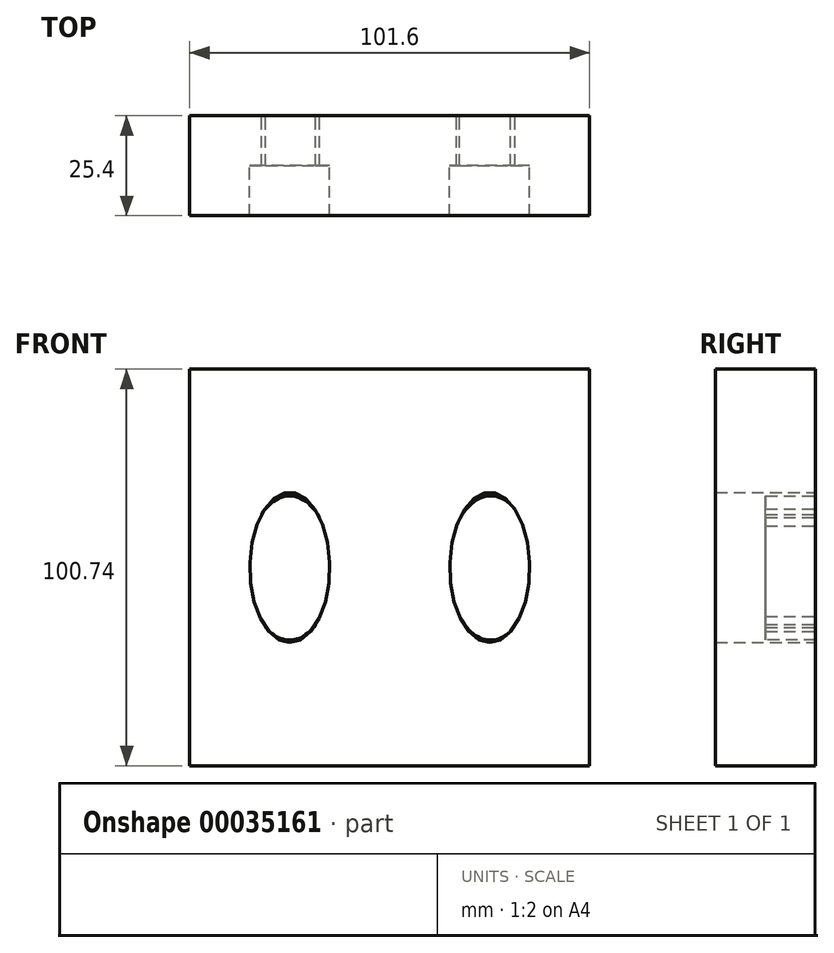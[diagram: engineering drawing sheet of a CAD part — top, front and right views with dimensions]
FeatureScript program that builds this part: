
annotation { "Feature Type Name" : "Feature", "Feature Type Description" : "" }
export const myFeature = defineFeature(function(context is Context, id is Id, definition is map)
    precondition{}
    {
        {
            var Q0;
            Q0=qCreatedBy(makeId("Front.planeOp"),FACE);
            var sketch = newSketch(context, id + "F0", { "sketchPlane" : qUnion([Q0])});
            skLineSegment(sketch, "E0.rect.bottom", {"start": v(50.8, -50.37) * mm, "end": v(-50.8, -50.37) * mm});
            skLineSegment(sketch, "E0.rect.top", {"start": v(50.8, 50.37) * mm, "end": v(-50.8, 50.37) * mm});
            skLineSegment(sketch, "E0.rect.left", {"start": v(50.8, -50.37) * mm, "end": v(50.8, 50.37) * mm});
            skLineSegment(sketch, "E0.rect.right", {"start": v(-50.8, -50.37) * mm, "end": v(-50.8, 50.37) * mm});
            skPoint(sketch, "E0.rect.middle", {"position": v(0, 0) * mm});
            skLineSegment(sketch, "E1", {"start": v(0, 50.37) * mm, "end": v(0, -50.37) * mm});
            skLineSegment(sketch, "E2", {"start": v(0, -50.37) * mm, "end": v(0, 50.37) * mm});
            skPoint(sketch, "E3.centerSnap0", {"position": v(-50.8, 0) * mm});
            skEllipse(sketch, "E4", {"center": v(-25.4, 0) * mm, "majorRadius": 19.05 * mm, "minorRadius": 10.16 * mm, "majorAxis": v(0, -1)});
            skEllipse(sketch, "E5.MirrorC", {"center": v(25.4, 0) * mm, "majorRadius": 19.05 * mm, "minorRadius": 10.16 * mm, "majorAxis": v(0, -1)});
            skSolve(sketch);
        }
        {
            var Q0;
            {var subQ2=sQuery(id+"F0.wireOp",EDGE,"E0.rect.right");Q0=makeQuery(id+"F0.imprint","IMPRINT",FACE,{"disambiguationData":[TD([[makeQuery(id+"F0.imprint","IMPRINT",EDGE,{"derivedFrom":subQ2}),-1.0]])]});}
            var Q1;
            {var subQ2=sQuery(id+"F0.wireOp",EDGE,"E0.rect.left");Q1=makeQuery(id+"F0.imprint","IMPRINT",FACE,{"disambiguationData":[TD([[makeQuery(id+"F0.imprint","IMPRINT",EDGE,{"derivedFrom":subQ2}),1.0]])]});}
            extrude(context, id + "F1", {"entities" : qUnion([Q0, Q1]), "depth" : 25.4 * mm});
        }
        {
            var Q0;
            Q0=qCreatedBy(makeId("Front.planeOp"),FACE);
            var sketch = newSketch(context, id + "F2", { "sketchPlane" : qUnion([Q0])});
            skLineSegment(sketch, "E6.rect.bottom", {"start": v(50.89, -50.5) * mm, "end": v(-50.71, -50.5) * mm});
            skLineSegment(sketch, "E6.rect.top", {"start": v(50.89, 50.23) * mm, "end": v(-50.71, 50.23) * mm});
            skLineSegment(sketch, "E6.rect.left", {"start": v(50.89, -50.5) * mm, "end": v(50.89, 50.23) * mm});
            skLineSegment(sketch, "E6.rect.right", {"start": v(-50.71, -50.5) * mm, "end": v(-50.71, 50.23) * mm});
            skPoint(sketch, "E6.rect.middle", {"position": v(0.09, -0.14) * mm});
            skLineSegment(sketch, "E7", {"start": v(0.09, 50.23) * mm, "end": v(0.09, -50.5) * mm});
            skLineSegment(sketch, "E8", {"start": v(0.09, -50.5) * mm, "end": v(0.09, 50.23) * mm});
            skPoint(sketch, "E9.centerSnap0", {"position": v(-50.71, -0.14) * mm});
            skEllipse(sketch, "E10", {"center": v(-25.44, -0.14) * mm, "majorRadius": 18.32 * mm, "minorRadius": 10.68 * mm, "majorAxis": v(0, -1)});
            skEllipse(sketch, "E11.MirrorC", {"center": v(25.62, -0.14) * mm, "majorRadius": 18.32 * mm, "minorRadius": 10.68 * mm, "majorAxis": v(0, -1)});
            skSolve(sketch);
        }
        {
            var Q0;
            Q0=makeQuery(id+"F2.imprint","IMPRINT",FACE,{"disambiguationData":[TD([[makeQuery(id+"F2.imprint","IMPRINT",EDGE,{"derivedFrom":sQuery(id+"F2.wireOp",EDGE,"E10")}),1.0]])]});
            var Q1;
            Q1=makeQuery(id+"F2.imprint","IMPRINT",FACE,{"disambiguationData":[TD([[makeQuery(id+"F2.imprint","IMPRINT",EDGE,{"derivedFrom":sQuery(id+"F2.wireOp",EDGE,"E11.MirrorC")}),1.0]])]});
            extrude(context, id + "F3", {"entities" : qUnion([Q0, Q1]), "operationType" : NewBodyOperationType.ADD, "depth" : 12.7 * mm});
        }
    });
